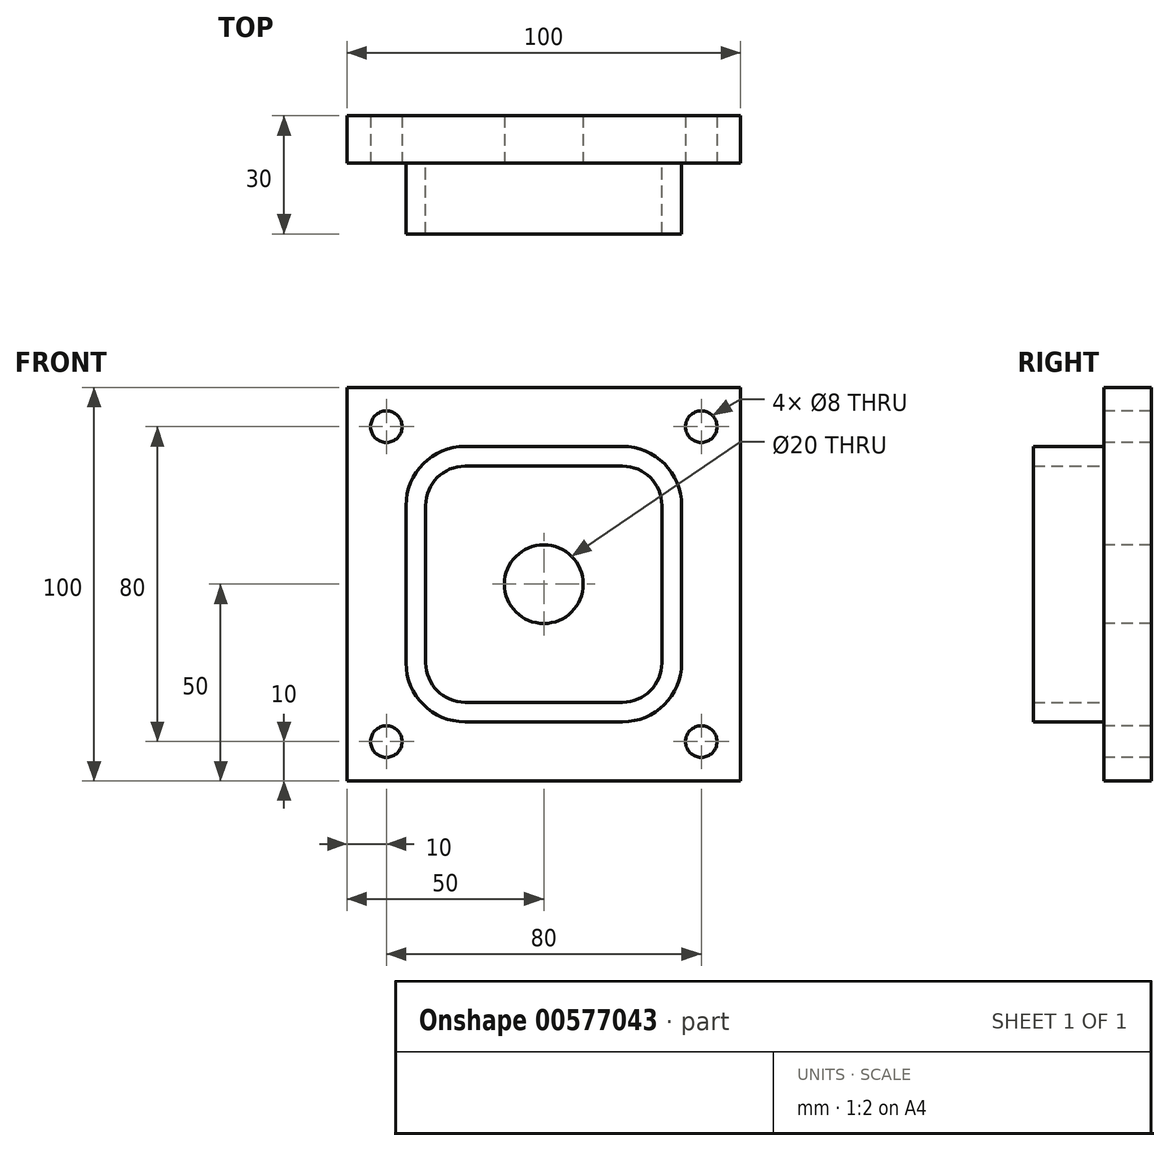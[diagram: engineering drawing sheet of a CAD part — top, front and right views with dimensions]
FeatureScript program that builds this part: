
annotation { "Feature Type Name" : "Feature", "Feature Type Description" : "" }
export const myFeature = defineFeature(function(context is Context, id is Id, definition is map)
    precondition{}
    {
        {
            var Q0;
            Q0=qCreatedBy(makeId("Front.planeOp"),FACE);
            var sketch = newSketch(context, id + "F0", { "sketchPlane" : qUnion([Q0])});
            skLineSegment(sketch, "E0.bottom", {"start": v(0, 0) * mm, "end": v(-100, 0) * mm});
            skLineSegment(sketch, "E0.top", {"start": v(0, 100) * mm, "end": v(-100, 100) * mm});
            skLineSegment(sketch, "E0.left", {"start": v(0, 0) * mm, "end": v(0, 100) * mm});
            skLineSegment(sketch, "E0.right", {"start": v(-100, 0) * mm, "end": v(-100, 100) * mm});
            skSolve(sketch);
        }
        {
            var Q0;
            Q0 = qSketchRegion(id + "F0", true);
            extrude(context, id + "F1", {"entities" : qUnion([Q0]), "oppositeDirection" : true, "depth" : 12 * mm, "offsetDistance" : 25 * mm});
        }
        {
            var Q0;
            Q0=makeQuery(id+"F1.opExtrude","CAP_FACE",FACE,{"disambiguationData":[OSD([sQuery(id+"F0.wireOp",EDGE,"E0.bottom"),sQuery(id+"F0.wireOp",EDGE,"E0.top"),sQuery(id+"F0.wireOp",EDGE,"E0.left"),sQuery(id+"F0.wireOp",EDGE,"E0.right")])],"isStart":true});
            var sketch = newSketch(context, id + "F2", { "sketchPlane" : qUnion([Q0])});
            skLineSegment(sketch, "E1.bottom", {"start": v(-10, 10) * mm, "end": v(-90, 10) * mm, "construction": true});
            skLineSegment(sketch, "E1.top", {"start": v(-10, 90) * mm, "end": v(-90, 90) * mm, "construction": true});
            skLineSegment(sketch, "E1.left", {"start": v(-10, 10) * mm, "end": v(-10, 90) * mm, "construction": true});
            skLineSegment(sketch, "E1.right", {"start": v(-90, 10) * mm, "end": v(-90, 90) * mm, "construction": true});
            skCircle(sketch, "E2", {"center": v(-90, 90) * mm, "radius": 4 * mm});
            skCircle(sketch, "E3", {"center": v(-10, 90) * mm, "radius": 4 * mm});
            skCircle(sketch, "E4", {"center": v(-10, 10) * mm, "radius": 4 * mm});
            skCircle(sketch, "E5", {"center": v(-90, 10) * mm, "radius": 4 * mm});
            skSolve(sketch);
        }
        {
            var Q0;
            Q0=makeQuery(id+"F2.imprint","IMPRINT",FACE,{"disambiguationData":[TD([[makeQuery(id+"F2.imprint","IMPRINT",EDGE,{"derivedFrom":sQuery(id+"F2.wireOp",EDGE,"E2")}),1.0]])]});
            var Q1;
            Q1=makeQuery(id+"F2.imprint","IMPRINT",FACE,{"disambiguationData":[TD([[makeQuery(id+"F2.imprint","IMPRINT",EDGE,{"derivedFrom":sQuery(id+"F2.wireOp",EDGE,"E3")}),1.0]])]});
            var Q2;
            Q2=makeQuery(id+"F2.imprint","IMPRINT",FACE,{"disambiguationData":[TD([[makeQuery(id+"F2.imprint","IMPRINT",EDGE,{"derivedFrom":sQuery(id+"F2.wireOp",EDGE,"E4")}),1.0]])]});
            var Q3;
            Q3=makeQuery(id+"F2.imprint","IMPRINT",FACE,{"disambiguationData":[TD([[makeQuery(id+"F2.imprint","IMPRINT",EDGE,{"derivedFrom":sQuery(id+"F2.wireOp",EDGE,"E5")}),1.0]])]});
            extrude(context, id + "F3", {"entities" : qUnion([Q0, Q1, Q2, Q3]), "operationType" : NewBodyOperationType.REMOVE, "oppositeDirection" : true, "depth" : 25 * mm, "offsetDistance" : 25 * mm});
        }
        {
            var Q0;
            Q0=makeQuery(id+"F1.opExtrude","CAP_FACE",FACE,{"disambiguationData":[OSD([sQuery(id+"F0.wireOp",EDGE,"E0.bottom"),sQuery(id+"F0.wireOp",EDGE,"E0.top"),sQuery(id+"F0.wireOp",EDGE,"E0.left"),sQuery(id+"F0.wireOp",EDGE,"E0.right")])],"isStart":true});
            var sketch = newSketch(context, id + "F4", { "sketchPlane" : qUnion([Q0])});
            skCircle(sketch, "E6", {"center": v(-50, 50) * mm, "radius": 10 * mm});
            skSolve(sketch);
        }
        {
            var Q0;
            Q0=makeQuery(id+"F4.imprint","IMPRINT",FACE,{"disambiguationData":[TD([[makeQuery(id+"F4.imprint","IMPRINT",EDGE,{"derivedFrom":sQuery(id+"F4.wireOp",EDGE,"E6")}),1.0]])]});
            extrude(context, id + "F5", {"entities" : qUnion([Q0]), "operationType" : NewBodyOperationType.REMOVE, "oppositeDirection" : true, "depth" : 25 * mm, "offsetDistance" : 25 * mm});
        }
        {
            var Q0;
            Q0=makeQuery(id+"F1.opExtrude","CAP_FACE",FACE,{"disambiguationData":[OSD([sQuery(id+"F0.wireOp",EDGE,"E0.bottom"),sQuery(id+"F0.wireOp",EDGE,"E0.top"),sQuery(id+"F0.wireOp",EDGE,"E0.left"),sQuery(id+"F0.wireOp",EDGE,"E0.right")])],"isStart":true});
            var sketch = newSketch(context, id + "F6", { "sketchPlane" : qUnion([Q0])});
            skLineSegment(sketch, "E7.bottom", {"start": v(-70, 85) * mm, "end": v(-30, 85) * mm});
            skLineSegment(sketch, "E7.top", {"start": v(-70, 15) * mm, "end": v(-30, 15) * mm});
            skLineSegment(sketch, "E7.left", {"start": v(-85, 70) * mm, "end": v(-85, 30) * mm});
            skLineSegment(sketch, "E7.right", {"start": v(-15, 70) * mm, "end": v(-15, 30) * mm});
            skPoint(sketch, "E8.visualSharp", {"position": v(-15, 85) * mm});
            skArc(sketch, "E8.filletArc", {"start": v(-15, 70) * mm, "mid": v(-19.4, 80.6) * mm, "end": v(-30, 85) * mm});
            skPoint(sketch, "E9.visualSharp", {"position": v(-85, 85) * mm});
            skArc(sketch, "E9.filletArc", {"start": v(-70, 85) * mm, "mid": v(-80.6, 80.6) * mm, "end": v(-85, 70) * mm});
            skPoint(sketch, "E10.visualSharp", {"position": v(-85, 15) * mm});
            skArc(sketch, "E10.filletArc", {"start": v(-85, 30) * mm, "mid": v(-80.6, 19.4) * mm, "end": v(-70, 15) * mm});
            skPoint(sketch, "E11.visualSharp", {"position": v(-15, 15) * mm});
            skArc(sketch, "E11.filletArc", {"start": v(-30, 15) * mm, "mid": v(-19.4, 19.4) * mm, "end": v(-15, 30) * mm});
            skSolve(sketch);
        }
        {
            var Q0;
            Q0=makeQuery(id+"F6.imprint","IMPRINT",FACE,{"disambiguationData":[TD([[makeQuery(id+"F6.imprint","IMPRINT",EDGE,{"derivedFrom":sQuery(id+"F6.wireOp",EDGE,"E7.bottom")}),1.0]])]});
            var sketch = newSketch(context, id + "F7", { "sketchPlane" : qUnion([Q0])});
            skLineSegment(sketch, "E12.bottom", {"start": v(-70, 80) * mm, "end": v(-30, 80) * mm});
            skLineSegment(sketch, "E12.top", {"start": v(-70, 20) * mm, "end": v(-30, 20) * mm});
            skLineSegment(sketch, "E12.left", {"start": v(-80, 70) * mm, "end": v(-80, 30) * mm});
            skLineSegment(sketch, "E12.right", {"start": v(-20, 70) * mm, "end": v(-20, 30) * mm});
            skPoint(sketch, "E13.visualSharp", {"position": v(-20, 80) * mm});
            skArc(sketch, "E13.filletArc", {"start": v(-20, 70) * mm, "mid": v(-22.93, 77.07) * mm, "end": v(-30, 80) * mm});
            skPoint(sketch, "E14.visualSharp", {"position": v(-20, 20) * mm});
            skArc(sketch, "E14.filletArc", {"start": v(-30, 20) * mm, "mid": v(-22.93, 22.93) * mm, "end": v(-20, 30) * mm});
            skPoint(sketch, "E15.visualSharp", {"position": v(-80, 20) * mm});
            skArc(sketch, "E15.filletArc", {"start": v(-80, 30) * mm, "mid": v(-77.07, 22.93) * mm, "end": v(-70, 20) * mm});
            skPoint(sketch, "E16.visualSharp", {"position": v(-80, 80) * mm});
            skArc(sketch, "E16.filletArc", {"start": v(-70, 80) * mm, "mid": v(-77.07, 77.07) * mm, "end": v(-80, 70) * mm});
            skSolve(sketch);
        }
        {
            var Q0;
            Q0 = qSketchRegion(id + "F6", true);
            extrude(context, id + "F8", {"entities" : qUnion([Q0]), "operationType" : NewBodyOperationType.ADD, "depth" : 18 * mm, "offsetDistance" : 25 * mm});
        }
        {
            var Q0;
            Q0 = qSketchRegion(id + "F7", true);
            extrude(context, id + "F9", {"entities" : qUnion([Q0]), "operationType" : NewBodyOperationType.REMOVE, "depth" : 25 * mm, "offsetDistance" : 25 * mm});
        }
    });
